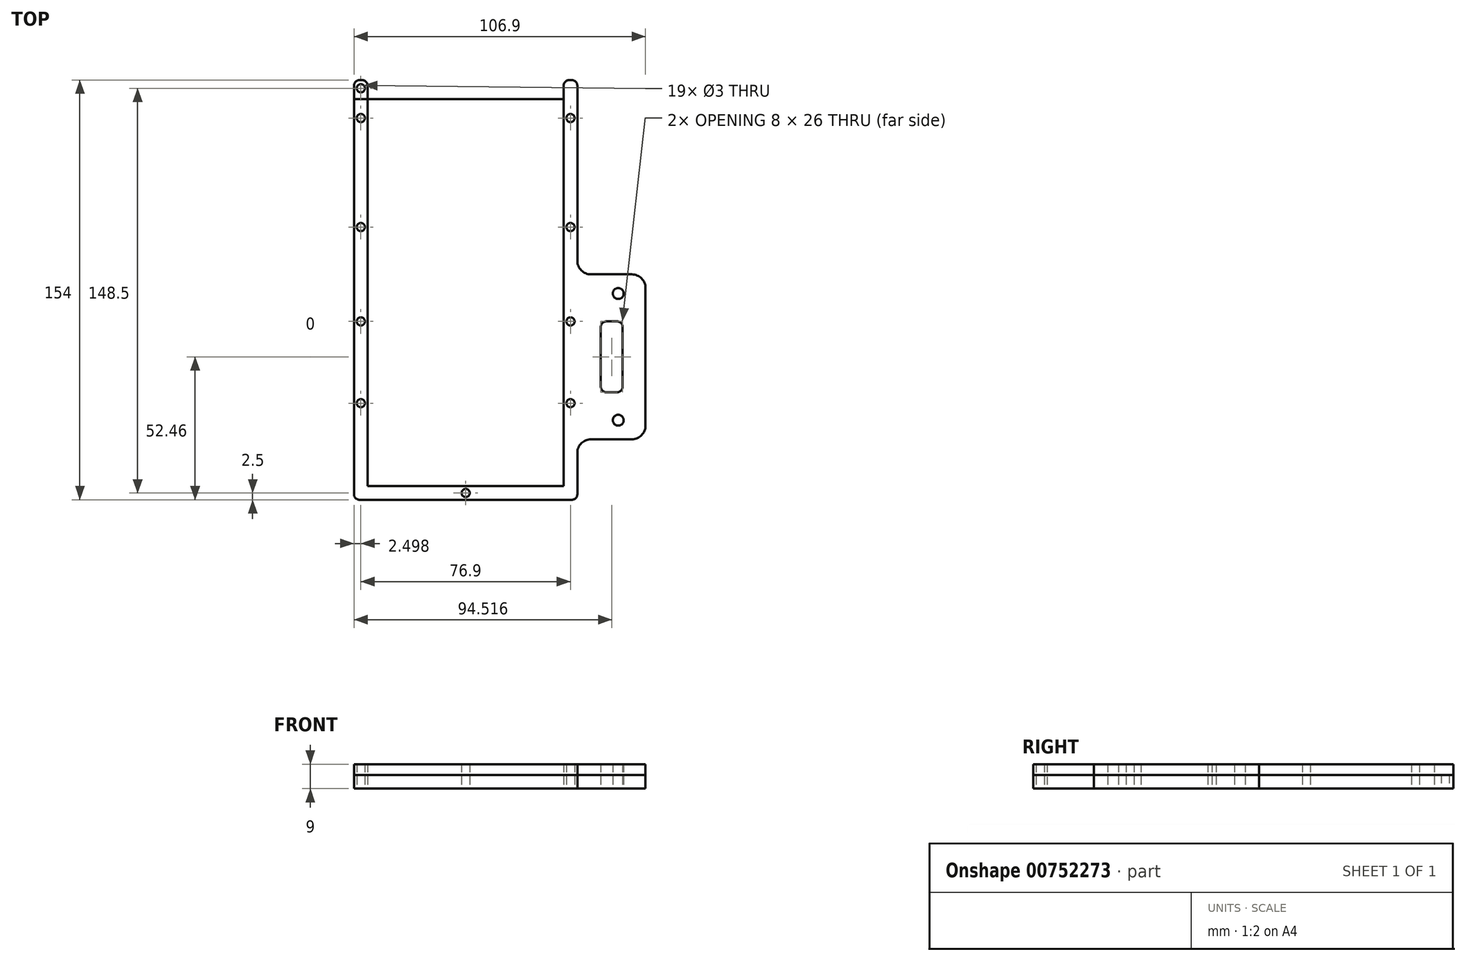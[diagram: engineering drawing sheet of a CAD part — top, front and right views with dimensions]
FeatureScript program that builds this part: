
annotation { "Feature Type Name" : "Feature", "Feature Type Description" : "" }
export const myFeature = defineFeature(function(context is Context, id is Id, definition is map)
    precondition{}
    {
        {
            var Q0;
            Q0=qCreatedBy(makeId("Top.planeOp"),FACE);
            var sketch = newSketch(context, id + "F0", { "sketchPlane" : qUnion([Q0])});
            skLineSegment(sketch, "E0.bottom", {"start": v(-46.15, 81.54) * mm, "end": v(25.75, 81.54) * mm});
            skLineSegment(sketch, "E0.top", {"start": v(-46.15, -60.46) * mm, "end": v(25.75, -60.46) * mm});
            skLineSegment(sketch, "E0.left", {"start": v(-46.15, 81.54) * mm, "end": v(-46.15, -60.46) * mm});
            skLineSegment(sketch, "E0.right", {"start": v(25.75, 81.54) * mm, "end": v(25.75, -60.46) * mm});
            skLineSegment(sketch, "E1.top", {"start": v(-48.15, 88.54) * mm, "end": v(-49.15, 88.54) * mm});
            skLineSegment(sketch, "E1.left", {"start": v(-46.15, -60.46) * mm, "end": v(-46.15, 86.54) * mm});
            skLineSegment(sketch, "E1.right", {"start": v(-51.15, -57.29) * mm, "end": v(-51.15, 86.54) * mm});
            skLineSegment(sketch, "E2.top", {"start": v(27.75, 88.54) * mm, "end": v(28.75, 88.54) * mm});
            skLineSegment(sketch, "E2.left", {"start": v(25.75, -60.46) * mm, "end": v(25.75, 86.54) * mm});
            skLineSegment(sketch, "E2.right", {"start": v(30.75, -60.46) * mm, "end": v(30.75, -48.25) * mm});
            skLineSegment(sketch, "E3.bottom", {"start": v(25.75, -60.46) * mm, "end": v(-46.15, -60.46) * mm});
            skLineSegment(sketch, "E3.top", {"start": v(28.75, -65.46) * mm, "end": v(-49.15, -65.46) * mm});
            skLineSegment(sketch, "E3.left", {"start": v(30.75, -60.46) * mm, "end": v(30.75, -63.46) * mm});
            skPoint(sketch, "E4.visualSharp", {"position": v(-51.15, 88.54) * mm});
            skArc(sketch, "E4.filletArc", {"start": v(-49.15, 88.54) * mm, "mid": v(-50.57, 87.95) * mm, "end": v(-51.15, 86.54) * mm});
            skPoint(sketch, "E5.visualSharp", {"position": v(30.75, 88.54) * mm});
            skArc(sketch, "E5.filletArc", {"start": v(30.75, 86.54) * mm, "mid": v(30.16, 87.95) * mm, "end": v(28.75, 88.54) * mm});
            skPoint(sketch, "E6.visualSharp", {"position": v(30.75, -65.46) * mm});
            skArc(sketch, "E6.filletArc", {"start": v(28.75, -65.46) * mm, "mid": v(30.16, -64.87) * mm, "end": v(30.75, -63.46) * mm});
            skPoint(sketch, "E7.visualSharp", {"position": v(-51.15, -65.46) * mm});
            skArc(sketch, "E7.filletArc", {"start": v(-51.15, -63.46) * mm, "mid": v(-50.57, -64.87) * mm, "end": v(-49.15, -65.46) * mm});
            skLineSegment(sketch, "E8", {"start": v(-51.15, -57.29) * mm, "end": v(-51.15, -63.46) * mm});
            skLineSegment(sketch, "E9", {"start": v(-46.15, 81.54) * mm, "end": v(-51.15, 81.54) * mm});
            skPoint(sketch, "E10.visualSharp", {"position": v(-46.15, 88.54) * mm});
            skArc(sketch, "E10.filletArc", {"start": v(-46.15, 86.54) * mm, "mid": v(-46.74, 87.95) * mm, "end": v(-48.15, 88.54) * mm});
            skPoint(sketch, "E11.visualSharp", {"position": v(25.75, 88.54) * mm});
            skArc(sketch, "E11.filletArc", {"start": v(27.75, 88.54) * mm, "mid": v(26.33, 87.95) * mm, "end": v(25.75, 86.54) * mm});
            skCircle(sketch, "E12", {"center": v(28.25, 74.61) * mm, "radius": 1.5 * mm});
            skPoint(sketch, "E12.centerSnap0", {"position": v(28.25, 88.54) * mm});
            skCircle(sketch, "E13", {"center": v(28.25, 34.61) * mm, "radius": 1.5 * mm});
            skCircle(sketch, "E14", {"center": v(28.25, 0) * mm, "radius": 1.5 * mm});
            skCircle(sketch, "E15", {"center": v(28.25, -30) * mm, "radius": 1.5 * mm});
            skCircle(sketch, "E16", {"center": v(-10.2, -62.96) * mm, "radius": 1.5 * mm});
            skPoint(sketch, "E16.centerSnap0", {"position": v(-21.13, -62.96) * mm});
            skPoint(sketch, "E16.centerSnap1", {"position": v(-10.2, -65.46) * mm});
            skPoint(sketch, "E17.orphan", {"position": v(-21.13, -65.46) * mm});
            skPoint(sketch, "E18.start.orphan", {"position": v(-21.13, -60.46) * mm});
            skCircle(sketch, "E19", {"center": v(-48.65, 74.61) * mm, "radius": 1.5 * mm});
            skPoint(sketch, "E19.centerSnap0", {"position": v(-48.65, 88.54) * mm});
            skCircle(sketch, "E20", {"center": v(-48.65, 34.61) * mm, "radius": 1.5 * mm});
            skCircle(sketch, "E21", {"center": v(-48.65, 0) * mm, "radius": 1.5 * mm});
            skCircle(sketch, "E22", {"center": v(-48.65, -30) * mm, "radius": 1.5 * mm});
            skCircle(sketch, "E23", {"center": v(45.75, 10.25) * mm, "radius": 2 * mm});
            skCircle(sketch, "E24", {"center": v(45.75, -36.25) * mm, "radius": 2 * mm});
            skLineSegment(sketch, "E25.bottom", {"start": v(35.75, 17.25) * mm, "end": v(50.75, 17.25) * mm});
            skLineSegment(sketch, "E25.top", {"start": v(35.75, -43.25) * mm, "end": v(50.75, -43.25) * mm});
            skLineSegment(sketch, "E25.right", {"start": v(55.75, 12.25) * mm, "end": v(55.75, -38.25) * mm});
            skLineSegment(sketch, "E26.trimOffspring", {"start": v(30.75, 22.25) * mm, "end": v(30.75, 86.54) * mm});
            skPoint(sketch, "E27.firstSnap0", {"position": v(55.75, -13) * mm});
            skLineSegment(sketch, "E27.bottom", {"start": v(47.37, -13) * mm, "end": v(39.37, -13) * mm});
            skLineSegment(sketch, "E27.top", {"start": v(45.37, 0) * mm, "end": v(41.37, 0) * mm});
            skLineSegment(sketch, "E27.left", {"start": v(47.37, -13) * mm, "end": v(47.37, -2) * mm});
            skLineSegment(sketch, "E27.right", {"start": v(39.37, -13) * mm, "end": v(39.37, -2) * mm});
            skLineSegment(sketch, "E28.top", {"start": v(45.37, -26) * mm, "end": v(41.37, -26) * mm});
            skLineSegment(sketch, "E28.left", {"start": v(47.37, -13) * mm, "end": v(47.37, -24) * mm});
            skLineSegment(sketch, "E28.right", {"start": v(39.37, -13) * mm, "end": v(39.37, -24) * mm});
            skPoint(sketch, "E29.visualSharp", {"position": v(39.37, 0) * mm});
            skArc(sketch, "E29.filletArc", {"start": v(41.37, 0) * mm, "mid": v(39.95, -0.59) * mm, "end": v(39.37, -2) * mm});
            skPoint(sketch, "E30.visualSharp", {"position": v(47.37, 0) * mm});
            skArc(sketch, "E30.filletArc", {"start": v(47.37, -2) * mm, "mid": v(46.78, -0.59) * mm, "end": v(45.37, 0) * mm});
            skPoint(sketch, "E31.visualSharp", {"position": v(39.37, -26) * mm});
            skArc(sketch, "E31.filletArc", {"start": v(39.37, -24) * mm, "mid": v(39.95, -25.41) * mm, "end": v(41.37, -26) * mm});
            skPoint(sketch, "E32.visualSharp", {"position": v(47.37, -26) * mm});
            skArc(sketch, "E32.filletArc", {"start": v(45.37, -26) * mm, "mid": v(46.78, -25.41) * mm, "end": v(47.37, -24) * mm});
            skPoint(sketch, "E33.visualSharp", {"position": v(55.75, 17.25) * mm});
            skArc(sketch, "E33.filletArc", {"start": v(55.75, 12.25) * mm, "mid": v(54.28, 15.79) * mm, "end": v(50.75, 17.25) * mm});
            skPoint(sketch, "E34.visualSharp", {"position": v(55.75, -43.25) * mm});
            skArc(sketch, "E34.filletArc", {"start": v(50.75, -43.25) * mm, "mid": v(54.28, -41.79) * mm, "end": v(55.75, -38.25) * mm});
            skPoint(sketch, "E35.visualSharp", {"position": v(30.75, -43.25) * mm});
            skArc(sketch, "E35.filletArc", {"start": v(35.75, -43.25) * mm, "mid": v(32.21, -44.71) * mm, "end": v(30.75, -48.25) * mm});
            skPoint(sketch, "E36.visualSharp", {"position": v(30.75, 17.25) * mm});
            skArc(sketch, "E36.filletArc", {"start": v(30.75, 22.25) * mm, "mid": v(32.21, 18.71) * mm, "end": v(35.75, 17.25) * mm});
            skCircle(sketch, "E37", {"center": v(-48.65, 85.54) * mm, "radius": 1.5 * mm});
            skSolve(sketch);
        }
        {
            var Q0;
            Q0=makeQuery(id+"F0.imprint","IMPRINT",FACE,{"disambiguationData":[TD([[makeQuery(id+"F0.imprint","IMPRINT",EDGE,{"derivedFrom":sQuery(id+"F0.wireOp",EDGE,"E2.top")}),-1.0]])]});
            extrude(context, id + "F1", {"entities" : qUnion([Q0]), "depth" : 9 * mm, "offsetDistance" : 25 * mm});
        }
        {
            var Q0;
            Q0 = qSketchRegion(id + "F0", true);
            extrude(context, id + "F2", {"entities" : qUnion([Q0]), "depth" : 5 * mm, "offsetDistance" : 25 * mm});
        }
    });
